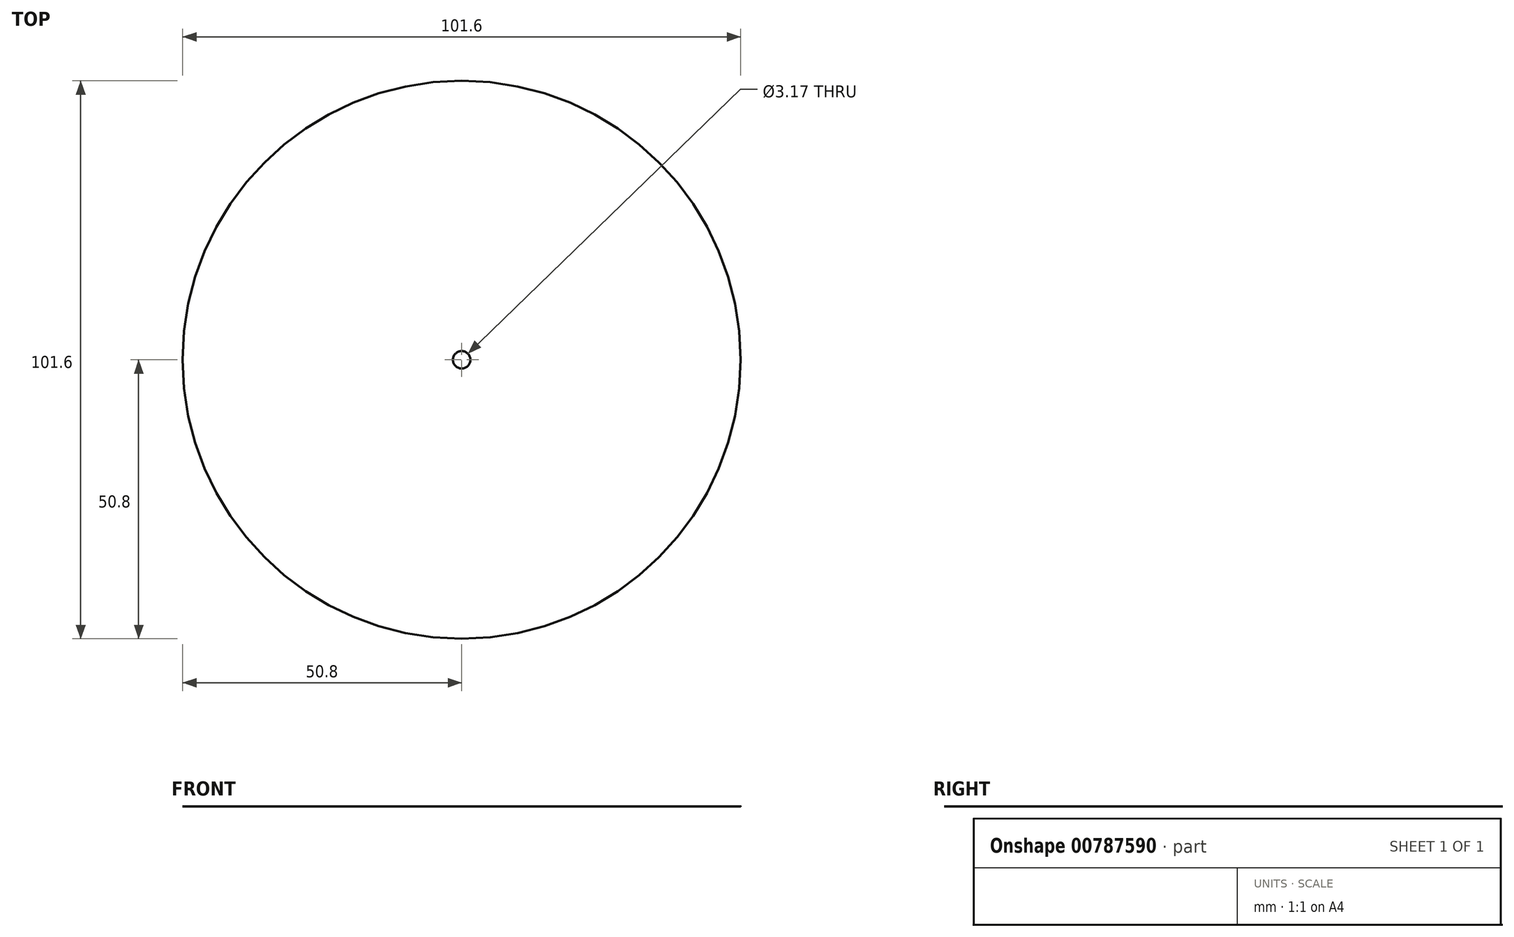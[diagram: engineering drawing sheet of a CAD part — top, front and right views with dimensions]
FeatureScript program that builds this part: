
annotation { "Feature Type Name" : "Feature", "Feature Type Description" : "" }
export const myFeature = defineFeature(function(context is Context, id is Id, definition is map)
    precondition{}
    {
        {
            var Q0;
            Q0=qCreatedBy(makeId("Top.planeOp"),FACE);
            var sketch = newSketch(context, id + "F0", { "sketchPlane" : qUnion([Q0])});
            skCircle(sketch, "E0", {"center": v(0, 0) * mm, "radius": 50.8 * mm});
            skCircle(sketch, "E1", {"center": v(0, 0) * mm, "radius": 6.35 * mm});
            skCircle(sketch, "E2", {"center": v(0, 0) * mm, "radius": 1.59 * mm});
            skSolve(sketch);
        }
        {
            var Q0;
            Q0=makeQuery(id+"F0.imprint","IMPRINT",FACE,{"disambiguationData":[TD([[makeQuery(id+"F0.imprint","IMPRINT",EDGE,{"derivedFrom":sQuery(id+"F0.wireOp",EDGE,"E0")}),1.0]])]});
            var Q1;
            Q1=makeQuery(id+"F0.imprint","IMPRINT",FACE,{"disambiguationData":[TD([[makeQuery(id+"F0.imprint","IMPRINT",EDGE,{"derivedFrom":sQuery(id+"F0.wireOp",EDGE,"E1")}),1.0]])]});
            extrude(context, id + "F1", {"entities" : qUnion([Q0, Q1]), "depth" : 1 / 406.4 * mm, "offsetDistance" : 25.4 * mm});
        }
    });
